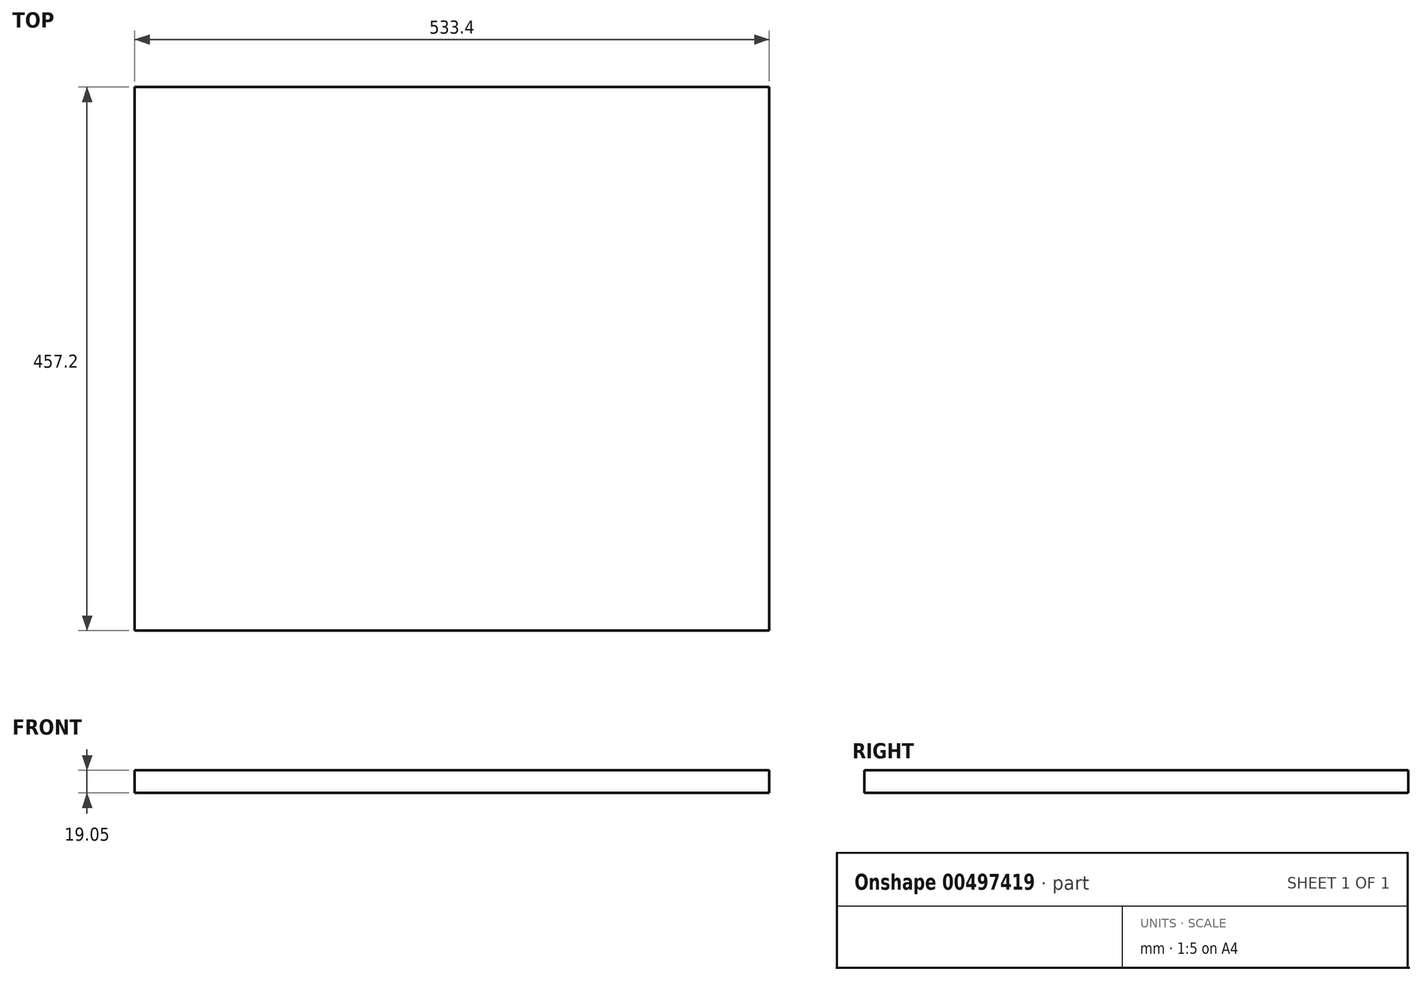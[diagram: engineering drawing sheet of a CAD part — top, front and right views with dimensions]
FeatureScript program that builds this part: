
annotation { "Feature Type Name" : "Feature", "Feature Type Description" : "" }
export const myFeature = defineFeature(function(context is Context, id is Id, definition is map)
    precondition{}
    {
        {
            var Q0;
            Q0=qCreatedBy(makeId("Front.planeOp"),FACE);
            var sketch = newSketch(context, id + "F0", { "sketchPlane" : qUnion([Q0])});
            skLineSegment(sketch, "E0.bottom", {"start": v(-214.22, 0) * mm, "end": v(319.18, 0) * mm});
            skLineSegment(sketch, "E0.top", {"start": v(-214.22, -19.05) * mm, "end": v(319.18, -19.05) * mm});
            skLineSegment(sketch, "E0.left", {"start": v(-214.22, 0) * mm, "end": v(-214.22, -19.05) * mm});
            skLineSegment(sketch, "E0.right", {"start": v(319.18, 0) * mm, "end": v(319.18, -19.05) * mm});
            skSolve(sketch);
        }
        {
            var Q0;
            Q0 = qSketchRegion(id + "F0", true);
            extrude(context, id + "F1", {"entities" : qUnion([Q0]), "depth" : 457.2 * mm});
        }
    });
